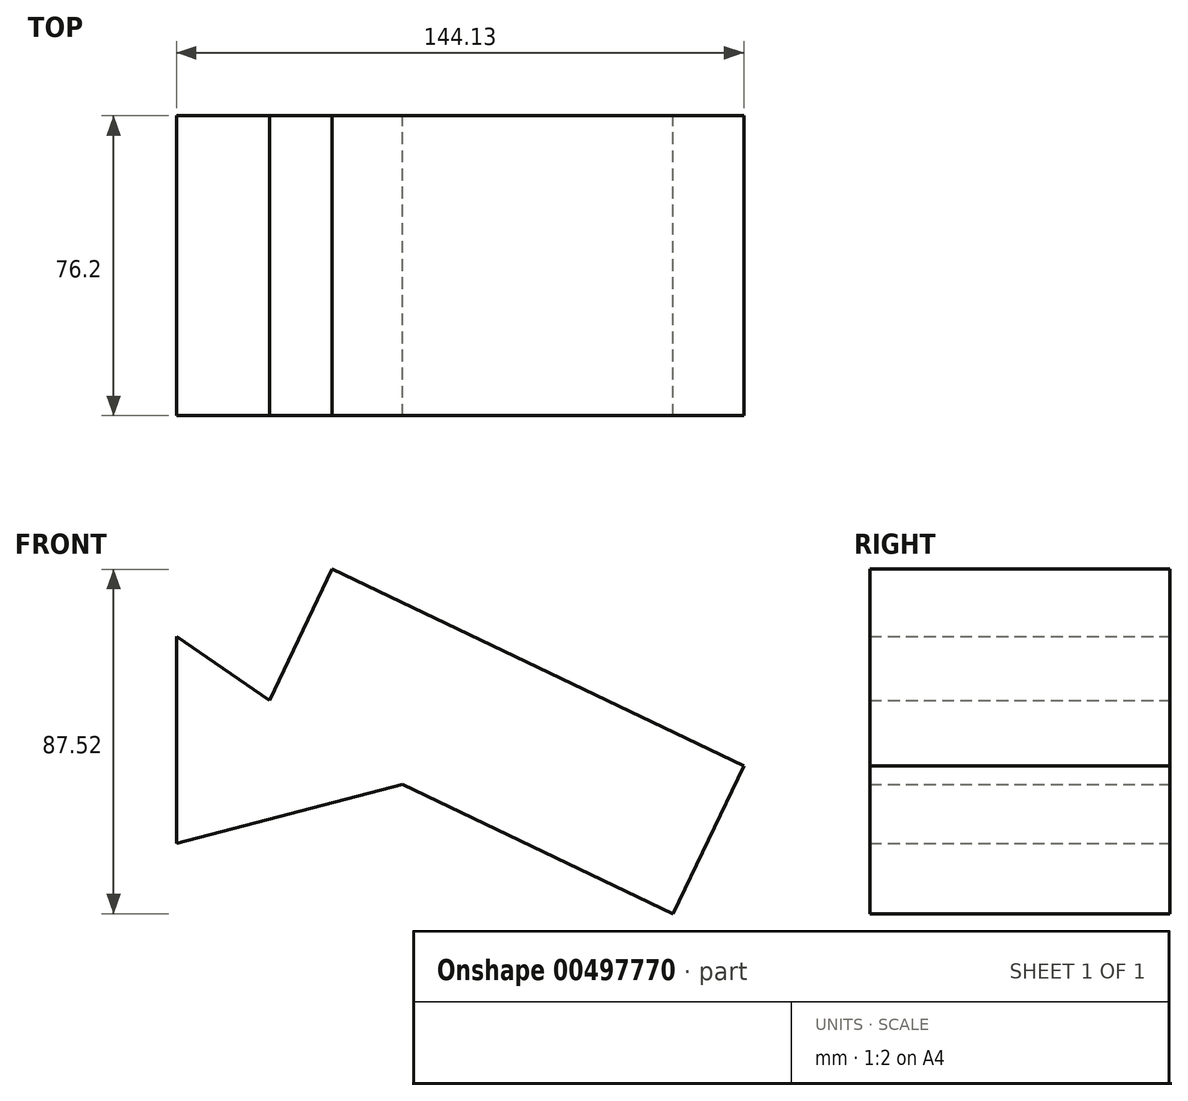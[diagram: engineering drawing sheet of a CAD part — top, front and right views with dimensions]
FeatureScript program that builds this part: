
annotation { "Feature Type Name" : "Feature", "Feature Type Description" : "" }
export const myFeature = defineFeature(function(context is Context, id is Id, definition is map)
    precondition{}
    {
        {
            var Q0;
            Q0=qCreatedBy(makeId("Front.planeOp"),FACE);
            var sketch = newSketch(context, id + "F0", { "sketchPlane" : qUnion([Q0])});
            skLineSegment(sketch, "E0", {"start": v(0, 0) * mm, "end": v(15.94, 33.32) * mm});
            skLineSegment(sketch, "E1", {"start": v(15.94, 33.32) * mm, "end": v(51.78, 16.18) * mm});
            skLineSegment(sketch, "E2", {"start": v(51.78, 16.18) * mm, "end": v(33.84, -21.32) * mm});
            skLineSegment(sketch, "E3", {"start": v(33.84, -21.32) * mm, "end": v(-23.6, -36.4) * mm});
            skLineSegment(sketch, "E4", {"start": v(-23.6, -36.4) * mm, "end": v(-23.6, 16.18) * mm});
            skLineSegment(sketch, "E5", {"start": v(-23.6, 16.18) * mm, "end": v(0, 0) * mm});
            skSolve(sketch);
        }
        {
            var Q0;
            Q0 = qSketchRegion(id + "F0", true);
            extrude(context, id + "F1", {"entities" : qUnion([Q0]), "depth" : 76.2 * mm});
        }
        {
            var Q0;
            Q0=makeQuery(id+"F1.opExtrude","SWEPT_FACE",FACE,{"disambiguationData":[OSD([sQuery(id+"F0.wireOp",EDGE,"E2")])]});
            extrude(context, id + "F2", {"entities" : qUnion([Q0]), "operationType" : NewBodyOperationType.ADD, "depth" : 76.2 * mm});
        }
    });
